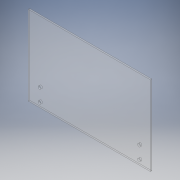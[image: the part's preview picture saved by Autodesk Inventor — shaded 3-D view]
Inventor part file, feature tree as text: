
AUTODESK INVENTOR PART (.ipt)
format: ipt  version: 2019 (Build 230136000, 136)  size: 112,128 bytes
history: native  units: in
note: dims shown in document units (in); Inventor stores cm internally (conversion verified against a paired STEP export)
features: sketch x2, extrude x1, hole x1
ambient origin geometry x8: Origin, YZ Plane, XZ Plane, XY Plane, X Axis, Y Axis, Z Axis, Center Point
bodies: Solid1 (feature_tree)
feature tree (4):
  extrude  "Extrusion1"  Depth=3.9in
  hole  "Hole1"  [1 undecoded]
  sketch  "Sketch1"  dims[d0=6.0in d1=3.9in]
  sketch  "Sketch2"  dims[d2=0.073in d3=0.0in d4=0.6299in d5=0.557in d6=0.557in d7=3.054in d8=0.6299in d9=0.557in d10=0.557in d11=3.054in d12=0.15in d13=0.75in d14=0.375in d15=0.25in d16=0.5635in d17=0.432in d18=0.8108in]
note: 1 required parameter value undecoded (feature->parameter linkage not recoverable at this tier; creation-order binding heuristic only, values carry confidence <= 0.55)
